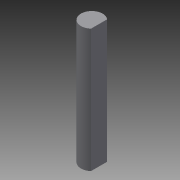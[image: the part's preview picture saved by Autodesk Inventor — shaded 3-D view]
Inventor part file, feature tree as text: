
AUTODESK INVENTOR PART (.ipt)
format: ipt  version: 2015 SP1 (Build 190203100, 203)  size: 69,120 bytes
history: native  units: in
note: dims shown in document units (in); Inventor stores cm internally (conversion verified against a paired STEP export)
features: extrude x1, sketch x1
ambient origin geometry x8: Origin, YZ Plane, XZ Plane, XY Plane, X Axis, Y Axis, Z Axis, Center Point
bodies: Solid1 (feature_tree)
feature tree (2):
  extrude  "Extrusion1"  Depth=34.1in
  sketch  "Sketch1"  dims[d0=3.0in d1=5.0in d2=34.1in d3=0.0in]
